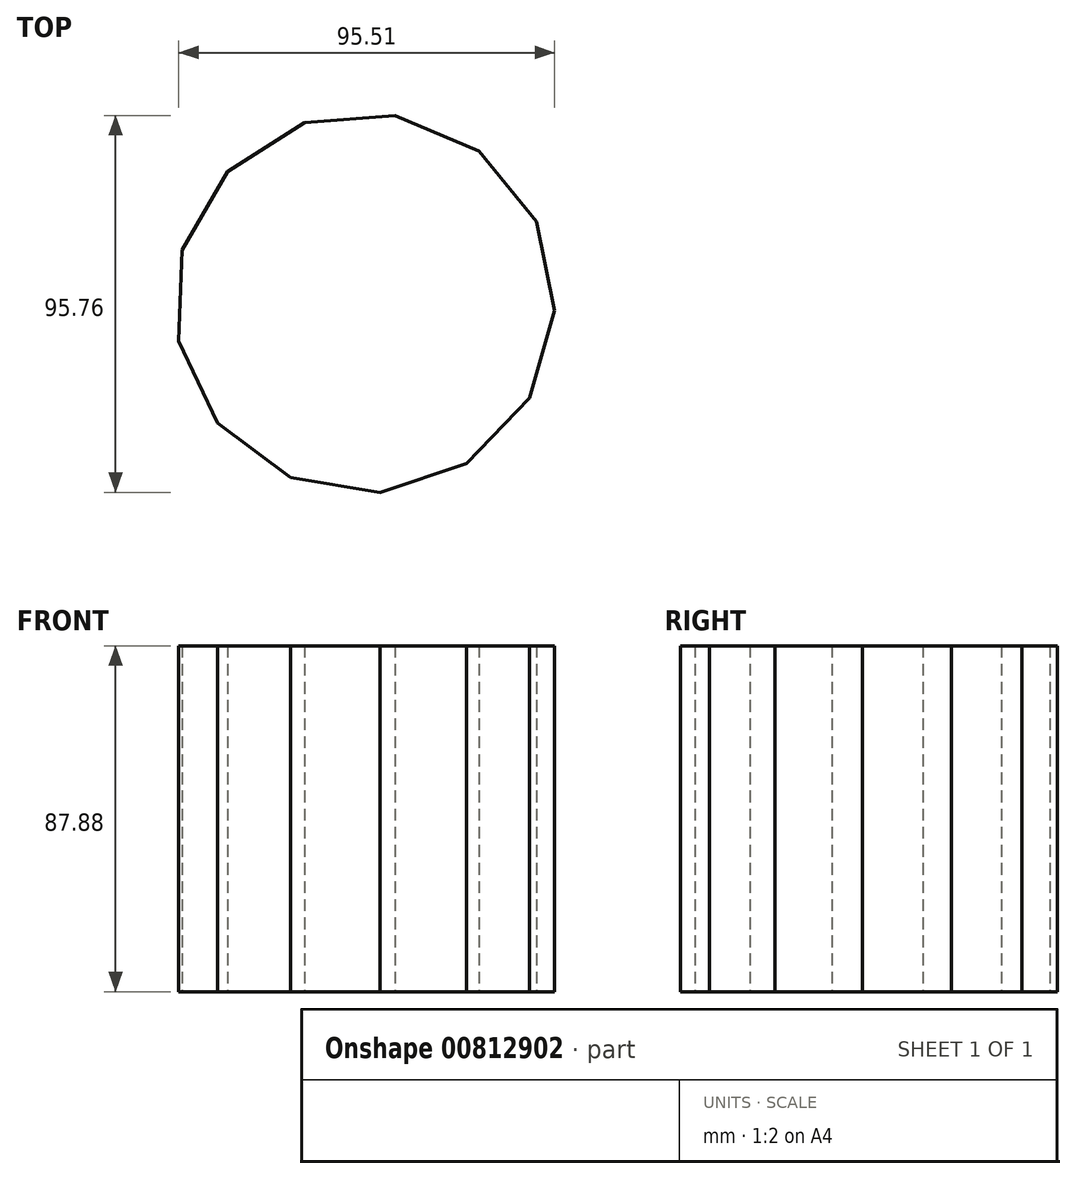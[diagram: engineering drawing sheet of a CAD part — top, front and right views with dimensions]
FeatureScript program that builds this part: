
annotation { "Feature Type Name" : "Feature", "Feature Type Description" : "" }
export const myFeature = defineFeature(function(context is Context, id is Id, definition is map)
    precondition{}
    {
        {
            var Q0;
            Q0=qCreatedBy(makeId("Top.planeOp"),FACE);
            var sketch = newSketch(context, id + "F0", { "sketchPlane" : qUnion([Q0])});
            skCircle(sketch, "E0.cCircle", {"center": v(0, 0) * mm, "radius": 46.86 * mm, "construction": true});
            skLineSegment(sketch, "E0.0", {"start": v(-37.37, -30.55) * mm, "end": v(-47.28, -9.69) * mm});
            skLineSegment(sketch, "E0.1", {"start": v(-47.28, -9.69) * mm, "end": v(-46.37, 13.4) * mm});
            skLineSegment(sketch, "E0.2", {"start": v(-46.37, 13.4) * mm, "end": v(-34.83, 33.41) * mm});
            skLineSegment(sketch, "E0.3", {"start": v(-34.83, 33.41) * mm, "end": v(-15.32, 45.77) * mm});
            skLineSegment(sketch, "E0.4", {"start": v(-15.32, 45.77) * mm, "end": v(7.71, 47.65) * mm});
            skLineSegment(sketch, "E0.5", {"start": v(7.71, 47.65) * mm, "end": v(28.97, 38.6) * mm});
            skLineSegment(sketch, "E0.6", {"start": v(28.97, 38.6) * mm, "end": v(43.6, 20.72) * mm});
            skLineSegment(sketch, "E0.7", {"start": v(43.6, 20.72) * mm, "end": v(48.23, -1.91) * mm});
            skLineSegment(sketch, "E0.8", {"start": v(48.23, -1.91) * mm, "end": v(41.82, -24.1) * mm});
            skLineSegment(sketch, "E0.9", {"start": v(41.82, -24.1) * mm, "end": v(25.82, -40.78) * mm});
            skLineSegment(sketch, "E0.10", {"start": v(25.82, -40.78) * mm, "end": v(3.92, -48.1) * mm});
            skLineSegment(sketch, "E0.11", {"start": v(3.92, -48.1) * mm, "end": v(-18.89, -44.42) * mm});
            skLineSegment(sketch, "E0.12", {"start": v(-18.89, -44.42) * mm, "end": v(-37.37, -30.55) * mm});
            skPoint(sketch, "E0.0.midPoint", {"position": v(-42.33, -20.12) * mm});
            skSolve(sketch);
        }
        {
            var Q0;
            Q0=makeQuery(id+"F0.imprint","IMPRINT",FACE,{"disambiguationData":[TD([[makeQuery(id+"F0.imprint","IMPRINT",EDGE,{"derivedFrom":sQuery(id+"F0.wireOp",EDGE,"E0.0")}),-1.0]])]});
            extrude(context, id + "F1", {"entities" : qUnion([Q0]), "endBound" : BoundingType.SYMMETRIC, "depth" : 87.88 * mm, "offsetDistance" : 25.4 * mm});
        }
    });
